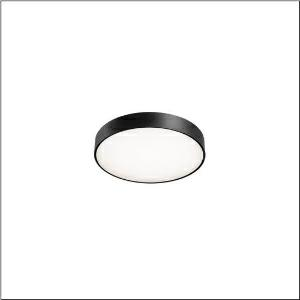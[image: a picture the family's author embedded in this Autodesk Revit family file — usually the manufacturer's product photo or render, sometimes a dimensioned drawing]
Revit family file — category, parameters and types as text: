
# Revit family: round_21_s_51mr34gd0421b
name_source: partatom
category: Lighting Fixtures
units: mm (PartAtom-declared; Revit-internal decimal feet)

## family parameters
Cut with Voids When Loaded = No
Host = Face
Light Source = No
Part Type = Normal
Room Calculation Point = No
Round Connector Dimension = Use Diameter
Shared = No

## types (1)
- Round 21 S (1 x LED, 3490 lm, 28 W, 4000K)
    Apparent Load = 28 VA
    CIE Flux Codes = 49 80 96 79 100
    Color Rendering = 80
    Color Temperature = 4000K
    Default Elevation = 1800 mm
    Description = Round 21 S, wall and ceiling luminaire, primary optical cover: cover, of PMMA, opal, light emission: direct/indirect distribution, primary light characteristic: symmetric, installation type: suspended mounting, surface-mounted, LED, rated luminous flux: 3.580lm, luminous efficacy: 118lm/W, light colour: 840, colour temperature: 4000K, with terminal, 5-pole, mains connection: 230V, AC, 50/60Hz, rated input power: 30W, housing, of aluminium, coated, black, diameter: 400mm, height: 62mm, protection rating (complete): IP40, insulation class (complete): insulation class I (protective earthing), certification: CE, impact resistance: IK04, permissible operating ambient temperature: -10..+35°C, packaging unit: 1 piece
    Height = 87 mm
    Lamp = 1 x LED
    Lamp Light Flux = 3490 lm
    Lamp Power = 28 W
    Lamp count = 1
    Length = 400 mm
    Luminous efficacy = 125 lm/W
    Manufacturer = Siteco
    ModVariant = No
    Model = 51MR34GD0421B
    Mounting Place = Ceiling
    Mounting Type = Surface mounted
    Number of Poles = 1
    OnlyDefault = Yes
    Power Factor = 1
    Product Name = Round 21 S
    Product group = wall and ceiling luminaire
    ProductGroupID = 302
    Protection Class = Protection class I
    Protection Degree = IP 40
    RLX_Detail_Level = 1
    RLX_Emergency_Light_Flux = 0 lm
    RLX_Emergency_Type = 0
    RLX_Emergency_Type_DB = No
    RlxData = <blob elided: 13825 chars, md5=22b34ec3>
    Socket = socket
    Standby Power = 0 W
    System Light Flux = 3490 lm
    System Power = 28 W
    Type Comments = Product without accessories
    Type Image = l_1258311.jpg
    URL = http://relux.com
    VarID = ---
    Voltage = 0 V
    Weight = 0.00 kg
    Width = 0 mm  [stored 0 ft]

note: [stored X ft] marks values corroborated as IEEE doubles in the binary element streams (Revit-internal decimal feet)

## geometry (parser evidence)
native form markers: Sweep x13
no freeform markers — native parametric forms only
